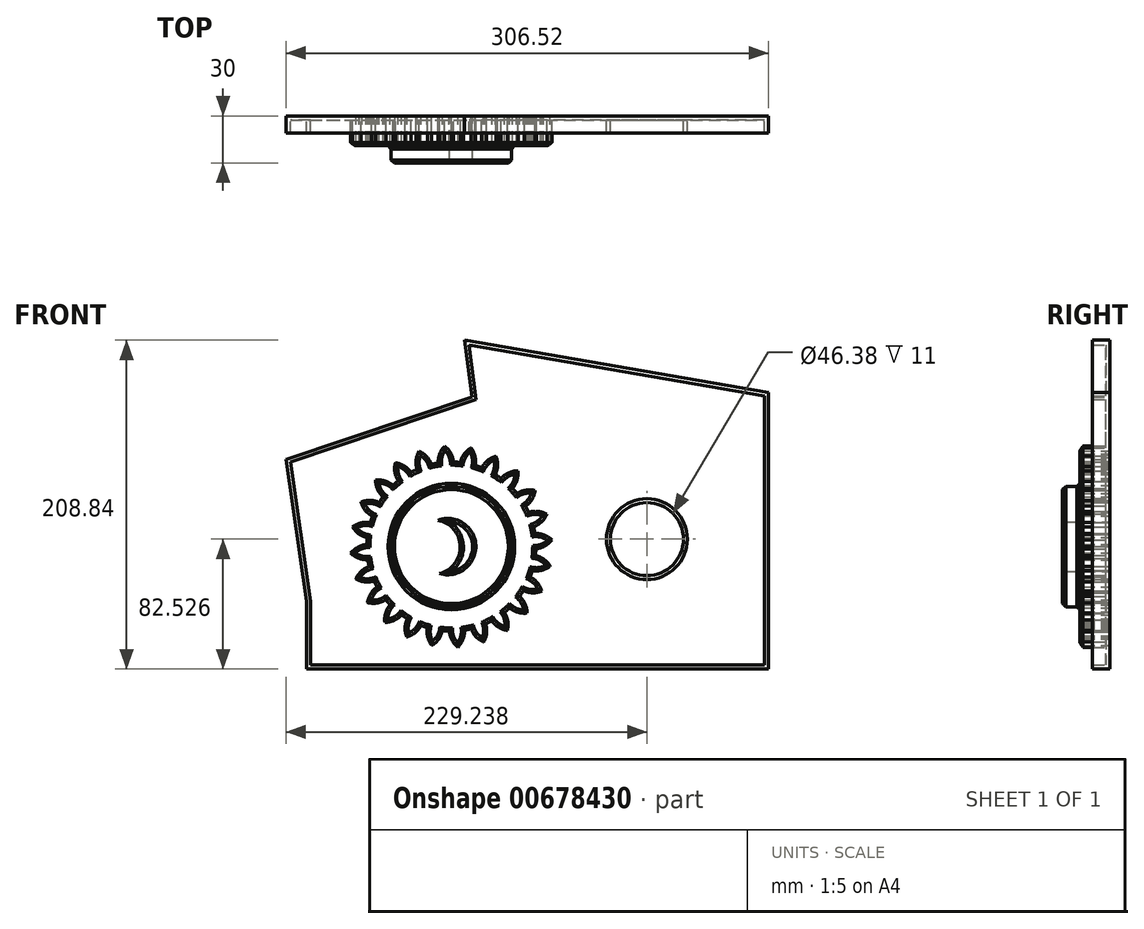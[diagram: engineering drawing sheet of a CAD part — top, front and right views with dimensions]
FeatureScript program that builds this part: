
annotation { "Feature Type Name" : "Feature", "Feature Type Description" : "" }
export const myFeature = defineFeature(function(context is Context, id is Id, definition is map)
    precondition{}
    {
        {
            var Q0;
            Q0=qCreatedBy(makeId("Front.planeOp"),FACE);
            var sketch = newSketch(context, id + "F0", { "sketchPlane" : qUnion([Q0])});
            skCircle(sketch, "E0", {"center": v(0, 0) * mm, "radius": 53.72 * mm});
            skCircle(sketch, "E1", {"center": v(0, 0) * mm, "radius": 58.67 * mm, "construction": true});
            skCircle(sketch, "E2", {"center": v(-1.68, 0) * mm, "radius": 63.5 * mm, "construction": true});
            skLineSegment(sketch, "E3", {"start": v(0, 0) * mm, "end": v(0, 73.25) * mm, "construction": true});
            skLineSegment(sketch, "E4", {"start": v(0, 0) * mm, "end": v(-5.3, 80.73) * mm, "construction": true});
            skCircle(sketch, "E5", {"center": v(0, 0) * mm, "radius": 53.72 * mm, "construction": true});
            skPoint(sketch, "E6.second.point", {"position": v(-45.4, 53.07) * mm});
            skPoint(sketch, "E6.third.point", {"position": v(-16.54, 31.13) * mm});
            skCircle(sketch, "E7", {"center": v(0, 58.67) * mm, "radius": 14.6 * mm, "construction": true});
            skCircle(sketch, "E8", {"center": v(-13.18, 52.37) * mm, "radius": 14.6 * mm, "construction": true});
            skLineSegment(sketch, "E9", {"start": v(0, 58.67) * mm, "end": v(-92.25, 41.51) * mm, "construction": true});
            skLineSegment(sketch, "E10", {"start": v(0, 58.67) * mm, "end": v(-92.84, 48.87) * mm, "construction": true});
            skArc(sketch, "E11", {"start": v(0, 58.67) * mm, "mid": v(-1.8, 61.52) * mm, "end": v(-4.19, 63.88) * mm});
            skArc(sketch, "E12", {"start": v(0, 46.07) * mm, "mid": v(1.41, 52.37) * mm, "end": v(0, 58.67) * mm});
            skArc(sketch, "E13.MirrorCS", {"start": v(-6.01, 45.68) * mm, "mid": v(-8.23, 51.74) * mm, "end": v(-7.66, 58.17) * mm});
            skArc(sketch, "E14.MirrorCS", {"start": v(-7.66, 58.17) * mm, "mid": v(-6.25, 61.22) * mm, "end": v(-4.19, 63.88) * mm});
            skCircle(sketch, "E15", {"center": v(0, 0) * mm, "radius": 38.2 * mm});
            skArc(sketch, "E16", {"start": v(0, -15.72) * mm, "mid": v(13.52, 0.5) * mm, "end": v(-1.04, 15.8) * mm});
            skArc(sketch, "E17", {"start": v(0, -15.72) * mm, "mid": v(7.64, 0.3) * mm, "end": v(-1.04, 15.8) * mm});
            skSolve(sketch);
        }
        {
            var Q0;
            {var subQ0=sQuery(id+"F0.wireOp",EDGE,"E0");var subQ1=makeQuery(id+"F0.imprint","INTERSECT",VERTEX,{"derivedFrom":[subQ0,sQuery(id+"F0.wireOp",EDGE,"E12")]});Q0=makeQuery(id+"F0.imprint","IMPRINT",FACE,{"disambiguationData":[TD([[makeQuery(id+"F0.imprint","IMPRINT",EDGE,{"disambiguationData":[TD([[subQ1,-1.0]])],"derivedFrom":subQ0}),1.0]])]});}
            var Q1;
            {var subQ5=sQuery(id+"F0.wireOp",EDGE,"E11");Q1=makeQuery(id+"F0.imprint","IMPRINT",FACE,{"disambiguationData":[TD([[makeQuery(id+"F0.imprint","IMPRINT",EDGE,{"derivedFrom":subQ5}),1.0]])]});}
            extrude(context, id + "F1", {"entities" : qUnion([Q0, Q1]), "depth" : 19 * mm, "offsetDistance" : 25 * mm});
        }
        {
            var Q0;
            Q0=makeQuery(id+"F1.opExtrude","SWEPT_BODY",BODY,{"disambiguationData":[OSD([sQuery(id+"F0.wireOp",EDGE,"E0"),sQuery(id+"F0.wireOp",EDGE,"E11"),sQuery(id+"F0.wireOp",EDGE,"E12"),sQuery(id+"F0.wireOp",EDGE,"E13.MirrorCS"),sQuery(id+"F0.wireOp",EDGE,"E14.MirrorCS")])]});
            var Q1;
            Q1=makeQuery(id+"F1.opExtrude","SWEPT_FACE",FACE,{"disambiguationData":[OSD([sQuery(id+"F0.wireOp",EDGE,"E0")])]});
            circularPattern(context, id + "F2", {"entities" : qUnion([Q0]), "axis" : qUnion([Q1]), "angle" : 360 * degree, "instanceCount" : 24, "oppositeDirection" : true, "equalSpace" : true});
        }
        {
            var Q0;
            Q0=makeQuery(id+"F0.imprint","IMPRINT",FACE,{"disambiguationData":[TD([[makeQuery(id+"F0.imprint","IMPRINT",EDGE,{"derivedFrom":sQuery(id+"F0.wireOp",EDGE,"E15")}),1.0]])]});
            extrude(context, id + "F3", {"entities" : qUnion([Q0]), "operationType" : NewBodyOperationType.ADD, "depth" : 30 * mm, "offsetDistance" : 25 * mm});
        }
        {
            var Q0;
            Q0=makeQuery(id+"F3.opExtrude","CAP_FACE",FACE,{"disambiguationData":[OSD([sQuery(id+"F0.wireOp",EDGE,"E15"),sQuery(id+"F0.wireOp",EDGE,"E16"),sQuery(id+"F0.wireOp",EDGE,"E17")])],"isStart":false});
            var Q1;
            {var subQ0=makeQuery(id+"F1.opExtrude","CAP_FACE",FACE,{"disambiguationData":[OSD([sQuery(id+"F0.wireOp",EDGE,"E0"),sQuery(id+"F0.wireOp",EDGE,"E11"),sQuery(id+"F0.wireOp",EDGE,"E12"),sQuery(id+"F0.wireOp",EDGE,"E13.MirrorCS"),sQuery(id+"F0.wireOp",EDGE,"E14.MirrorCS"),sQuery(id+"F0.wireOp",EDGE,"E15")])],"isStart":false});Q1=makeQuery(id+"F3.boolean.opBoolean","MERGE",FACE,{"derivedFrom":[subQ0,makeQuery(id+"F2.opPattern","COPY",FACE,{"derivedFrom":subQ0,"instanceName":"1"}),makeQuery(id+"F2.opPattern","COPY",FACE,{"derivedFrom":subQ0,"instanceName":"2"}),makeQuery(id+"F2.opPattern","COPY",FACE,{"derivedFrom":subQ0,"instanceName":"3"}),makeQuery(id+"F2.opPattern","COPY",FACE,{"derivedFrom":subQ0,"instanceName":"4"}),makeQuery(id+"F2.opPattern","COPY",FACE,{"derivedFrom":subQ0,"instanceName":"5"}),makeQuery(id+"F2.opPattern","COPY",FACE,{"derivedFrom":subQ0,"instanceName":"6"}),makeQuery(id+"F2.opPattern","COPY",FACE,{"derivedFrom":subQ0,"instanceName":"7"}),makeQuery(id+"F2.opPattern","COPY",FACE,{"derivedFrom":subQ0,"instanceName":"8"}),makeQuery(id+"F2.opPattern","COPY",FACE,{"derivedFrom":subQ0,"instanceName":"9"}),makeQuery(id+"F2.opPattern","COPY",FACE,{"derivedFrom":subQ0,"instanceName":"10"}),makeQuery(id+"F2.opPattern","COPY",FACE,{"derivedFrom":subQ0,"instanceName":"11"}),makeQuery(id+"F2.opPattern","COPY",FACE,{"derivedFrom":subQ0,"instanceName":"12"}),makeQuery(id+"F2.opPattern","COPY",FACE,{"derivedFrom":subQ0,"instanceName":"13"}),makeQuery(id+"F2.opPattern","COPY",FACE,{"derivedFrom":subQ0,"instanceName":"14"}),makeQuery(id+"F2.opPattern","COPY",FACE,{"derivedFrom":subQ0,"instanceName":"15"}),makeQuery(id+"F2.opPattern","COPY",FACE,{"derivedFrom":subQ0,"instanceName":"16"}),makeQuery(id+"F2.opPattern","COPY",FACE,{"derivedFrom":subQ0,"instanceName":"17"}),makeQuery(id+"F2.opPattern","COPY",FACE,{"derivedFrom":subQ0,"instanceName":"18"}),makeQuery(id+"F2.opPattern","COPY",FACE,{"derivedFrom":subQ0,"instanceName":"19"}),makeQuery(id+"F2.opPattern","COPY",FACE,{"derivedFrom":subQ0,"instanceName":"20"}),makeQuery(id+"F2.opPattern","COPY",FACE,{"derivedFrom":subQ0,"instanceName":"21"}),makeQuery(id+"F2.opPattern","COPY",FACE,{"derivedFrom":subQ0,"instanceName":"22"}),makeQuery(id+"F2.opPattern","COPY",FACE,{"derivedFrom":subQ0,"instanceName":"23"})]});}
            chamfer(context, id + "F4", {"entities" : qUnion([Q0, Q1]), "width" : 2 * mm, "tangentPropagation" : true});
        }
        {
            var Q0;
            Q0=qCreatedBy(makeId("Front.planeOp"),FACE);
            var sketch = newSketch(context, id + "F5", { "sketchPlane" : qUnion([Q0])});
            skLineSegment(sketch, "E18", {"start": v(-92.02, -34.88) * mm, "end": v(-92.02, -77.76) * mm});
            skLineSegment(sketch, "E19", {"start": v(-92.02, -77.76) * mm, "end": v(201.5, -77.76) * mm});
            skLineSegment(sketch, "E20", {"start": v(201.5, -77.76) * mm, "end": v(201.5, 97.78) * mm});
            skLineSegment(sketch, "E21", {"start": v(-92.02, -34.88) * mm, "end": v(-105.02, 55.36) * mm});
            skLineSegment(sketch, "E22", {"start": v(-105.02, 55.36) * mm, "end": v(12.99, 95.1) * mm});
            skLineSegment(sketch, "E23", {"start": v(8.36, 131.08) * mm, "end": v(12.99, 95.1) * mm});
            skLineSegment(sketch, "E24", {"start": v(201.5, 97.78) * mm, "end": v(8.36, 131.08) * mm});
            skCircle(sketch, "E25", {"center": v(124.22, 4.77) * mm, "radius": 23.2 * mm});
            skSolve(sketch);
        }
        {
            var Q0;
            Q0=makeQuery(id+"F5.imprint","IMPRINT",FACE,{"disambiguationData":[TD([[makeQuery(id+"F5.imprint","IMPRINT",EDGE,{"derivedFrom":sQuery(id+"F5.wireOp",EDGE,"E18")}),1.0]])]});
            extrude(context, id + "F6", {"entities" : qUnion([Q0]), "depth" : 11 * mm, "offsetDistance" : 25 * mm});
        }
        {
            var Q0;
            Q0=makeQuery(id+"F6.opExtrude","CAP_FACE",FACE,{"disambiguationData":[OSD([sQuery(id+"F5.wireOp",EDGE,"E18"),sQuery(id+"F5.wireOp",EDGE,"E19"),sQuery(id+"F5.wireOp",EDGE,"E20"),sQuery(id+"F5.wireOp",EDGE,"E21"),sQuery(id+"F5.wireOp",EDGE,"E22"),sQuery(id+"F5.wireOp",EDGE,"E23"),sQuery(id+"F5.wireOp",EDGE,"E24")])],"isStart":false});
            shell(context, id + "F7", {"entities" : qUnion([Q0]), "thickness" : 2.5 * mm});
        }
    });
